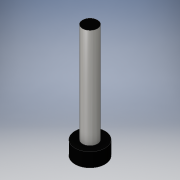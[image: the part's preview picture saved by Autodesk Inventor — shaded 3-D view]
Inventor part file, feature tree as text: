
AUTODESK INVENTOR PART (.ipt)
format: ipt  version: 2016 (Build 200138000, 138)  size: 100,864 bytes
history: native  units: in
note: dims shown in document units (in); Inventor stores cm internally (conversion verified against a paired STEP export)
features: extrude x2, sketch x2
ambient origin geometry x8: Origin, YZ Plane, XZ Plane, XY Plane, X Axis, Y Axis, Z Axis, Center Point
bodies: Solid1 (feature_tree)
feature tree (4):
  extrude  "Extrusion1"  Depth=0.1102in TaperAngle=0.0deg
  extrude  "Extrusion2"  Depth=0.7874in TaperAngle=0.0deg
  sketch  "Sketch1"  dims[d0=0.2362in d1=0.1102in d2=0.0in]
  sketch  "Sketch2"  dims[d3=0.1181in d4=0.7874in d5=0.0in]
